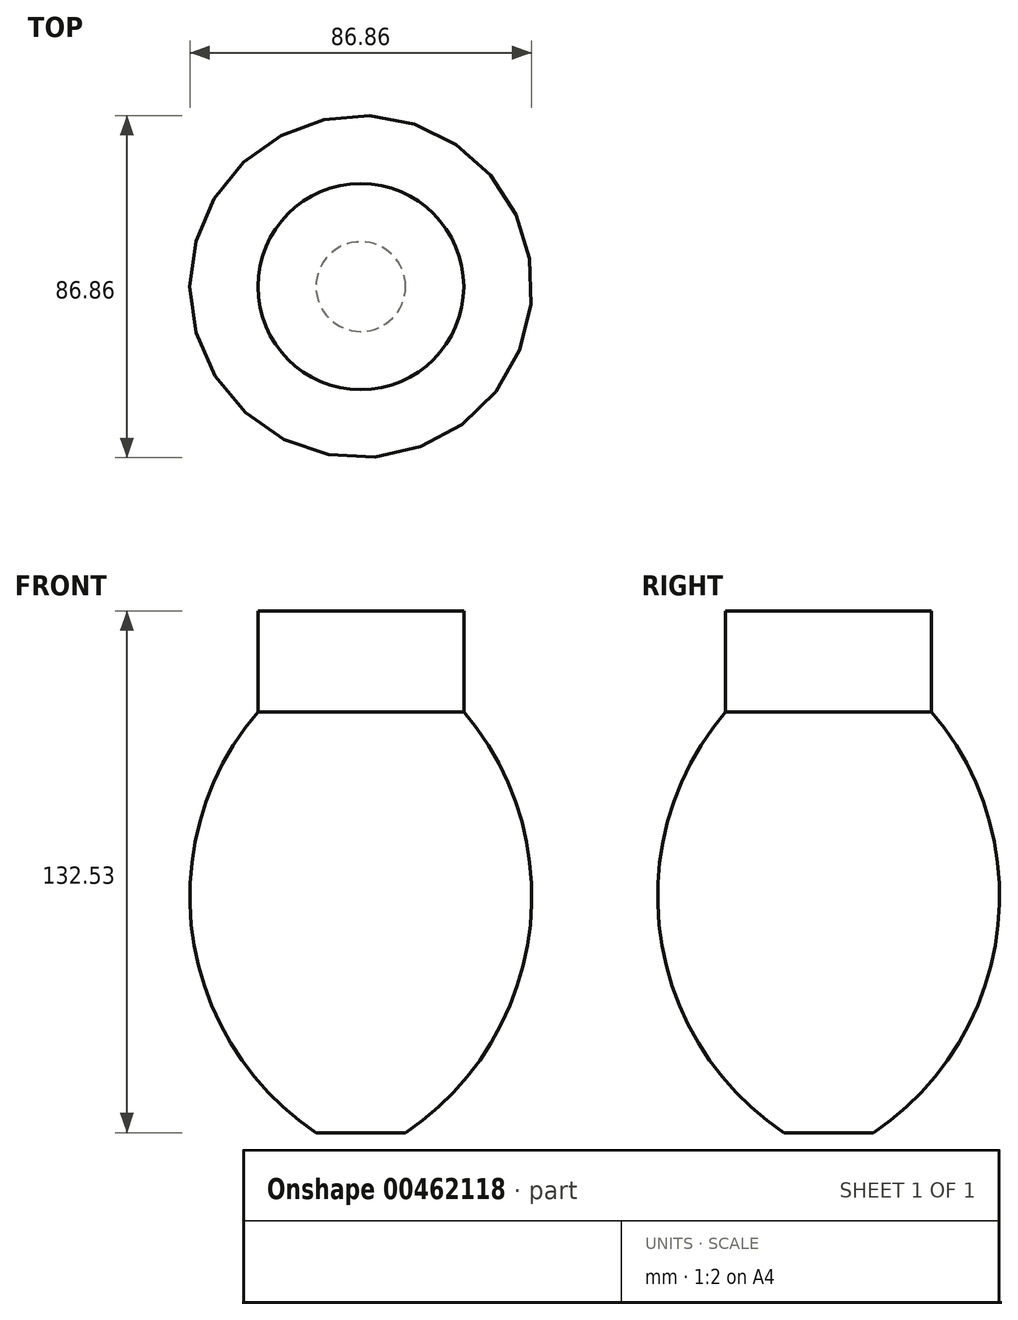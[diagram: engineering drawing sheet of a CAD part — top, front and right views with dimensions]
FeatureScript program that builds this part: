
annotation { "Feature Type Name" : "Feature", "Feature Type Description" : "" }
export const myFeature = defineFeature(function(context is Context, id is Id, definition is map)
    precondition{}
    {
        {
            var Q0;
            Q0=qCreatedBy(makeId("Front.planeOp"),FACE);
            var sketch = newSketch(context, id + "F0", { "sketchPlane" : qUnion([Q0])});
            skLineSegment(sketch, "E0", {"start": v(0, -76.22) * mm, "end": v(0, 73.94) * mm});
            skLineSegment(sketch, "E1", {"start": v(0, 73.94) * mm, "end": v(26.16, 73.94) * mm});
            skLineSegment(sketch, "E2", {"start": v(26.16, 73.94) * mm, "end": v(26.16, 48.35) * mm});
            skArc(sketch, "E3", {"start": v(11.38, -58.59) * mm, "mid": v(3.1, -65.73) * mm, "end": v(0, -76.22) * mm});
            skArc(sketch, "E4", {"start": v(11.38, -58.59) * mm, "mid": v(42.75, -8.44) * mm, "end": v(26.16, 48.35) * mm});
            skSolve(sketch);
        }
        {
            var Q0;
            Q0=makeQuery(id+"F0.imprint","IMPRINT",FACE,{"disambiguationData":[TD([[makeQuery(id+"F0.imprint","IMPRINT",EDGE,{"derivedFrom":sQuery(id+"F0.wireOp",EDGE,"E0")}),-1.0]])]});
            var Q1;
            Q1=sQuery(id+"F0.wireOp",EDGE,"E0");
            revolve(context, id + "F1", {"entities" : qUnion([Q0]), "axis" : qUnion([Q1]), "revolveType" : RevolveType.FULL});
        }
    });
